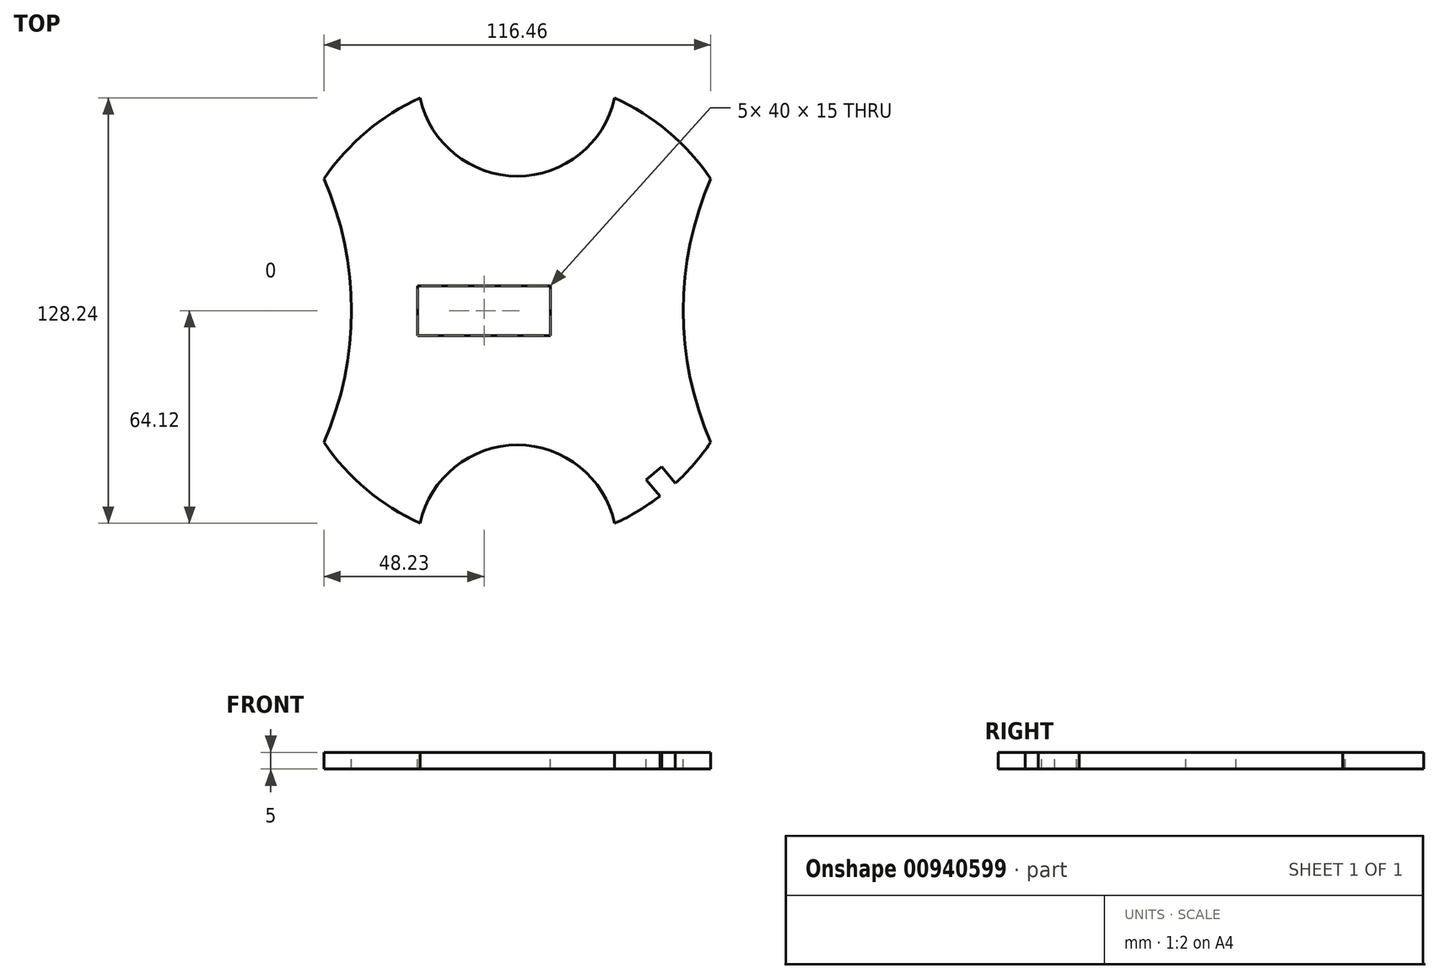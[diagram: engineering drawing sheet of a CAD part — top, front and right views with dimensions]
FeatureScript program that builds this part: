
annotation { "Feature Type Name" : "Feature", "Feature Type Description" : "" }
export const myFeature = defineFeature(function(context is Context, id is Id, definition is map)
    precondition{}
    {
        {
            var Q0;
            Q0=qCreatedBy(makeId("Top.planeOp"),FACE);
            var sketch = newSketch(context, id + "F0", { "sketchPlane" : qUnion([Q0])});
            skCircle(sketch, "E0", {"center": v(0, 0) * mm, "radius": 70.5 * mm});
            skSolve(sketch);
        }
        {
            var Q0;
            Q0 = qSketchRegion(id + "F0", true);
            extrude(context, id + "F1", {"entities" : qUnion([Q0]), "depth" : 5 * mm, "offsetDistance" : 25 * mm});
        }
        {
            var Q0;
            Q0=makeQuery(id+"F1.opExtrude","CAP_FACE",FACE,{"disambiguationData":[OSD([sQuery(id+"F0.wireOp",EDGE,"E0")])],"isStart":false});
            var sketch = newSketch(context, id + "F2", { "sketchPlane" : qUnion([Q0])});
            skLineSegment(sketch, "E1.bottom", {"start": v(-30, 7.5) * mm, "end": v(10, 7.5) * mm});
            skLineSegment(sketch, "E1.top", {"start": v(-30, -7.5) * mm, "end": v(10, -7.5) * mm});
            skLineSegment(sketch, "E1.left", {"start": v(-30, 7.5) * mm, "end": v(-30, -7.5) * mm});
            skLineSegment(sketch, "E1.right", {"start": v(10, 7.5) * mm, "end": v(10, -7.5) * mm});
            skSolve(sketch);
        }
        {
            var Q0;
            Q0 = qSketchRegion(id + "F2", true);
            extrude(context, id + "F3", {"entities" : qUnion([Q0]), "operationType" : NewBodyOperationType.REMOVE, "oppositeDirection" : true, "depth" : 25 * mm, "offsetDistance" : 25 * mm});
        }
        {
            var Q0;
            Q0=makeQuery(id+"F1.opExtrude","CAP_FACE",FACE,{"disambiguationData":[OSD([sQuery(id+"F0.wireOp",EDGE,"E0")])],"isStart":false});
            var sketch = newSketch(context, id + "F4", { "sketchPlane" : qUnion([Q0])});
            skLineSegment(sketch, "E2", {"start": v(0, -70.5) * mm, "end": v(0, 70.5) * mm, "construction": true});
            skCircle(sketch, "E3", {"center": v(0, 70.5) * mm, "radius": 30 * mm});
            skCircle(sketch, "E4", {"center": v(0, -70.5) * mm, "radius": 30 * mm});
            skLineSegment(sketch, "E5", {"start": v(-150, 0) * mm, "end": v(150, 0) * mm, "construction": true});
            skCircle(sketch, "E6", {"center": v(150, 0) * mm, "radius": 100 * mm});
            skCircle(sketch, "E7", {"center": v(-150, 0) * mm, "radius": 100 * mm});
            skSolve(sketch);
        }
        {
            var Q0;
            {var subQ0=sQuery(id+"F4.wireOp",EDGE,"E3");var subQ1=makeQuery(id+"F1.opExtrude","CAP_EDGE",EDGE,{"disambiguationData":[OSD([sQuery(id+"F0.wireOp",EDGE,"E0")])],"isStart":false});var subQ2=makeQuery(id+"F4.imprint","INTERSECT",VERTEX,{"disambiguationData":[OD(0.0)],"derivedFrom":[subQ1,subQ0]});Q0=makeQuery(id+"F4.imprint","IMPRINT",FACE,{"disambiguationData":[TD([[makeQuery(id+"F4.imprint","IMPRINT",EDGE,{"disambiguationData":[TD([[subQ2,-1.0]])],"derivedFrom":subQ0}),1.0]])]});}
            var Q1;
            {var subQ0=sQuery(id+"F4.wireOp",EDGE,"E7");var subQ1=makeQuery(id+"F1.opExtrude","CAP_EDGE",EDGE,{"disambiguationData":[OSD([sQuery(id+"F0.wireOp",EDGE,"E0")])],"isStart":false});var subQ2=makeQuery(id+"F4.imprint","INTERSECT",VERTEX,{"disambiguationData":[OD(0.0)],"derivedFrom":[subQ1,subQ0]});Q1=makeQuery(id+"F4.imprint","IMPRINT",FACE,{"disambiguationData":[TD([[makeQuery(id+"F4.imprint","IMPRINT",EDGE,{"disambiguationData":[TD([[subQ2,-1.0]])],"derivedFrom":subQ0}),1.0]])]});}
            var Q2;
            {var subQ0=sQuery(id+"F4.wireOp",EDGE,"E4");var subQ1=makeQuery(id+"F1.opExtrude","CAP_EDGE",EDGE,{"disambiguationData":[OSD([sQuery(id+"F0.wireOp",EDGE,"E0")])],"isStart":false});var subQ2=makeQuery(id+"F4.imprint","INTERSECT",VERTEX,{"disambiguationData":[OD(0.0)],"derivedFrom":[subQ1,subQ0]});Q2=makeQuery(id+"F4.imprint","IMPRINT",FACE,{"disambiguationData":[TD([[makeQuery(id+"F4.imprint","IMPRINT",EDGE,{"disambiguationData":[TD([[subQ2,1.0]])],"derivedFrom":subQ0}),1.0]])]});}
            var Q3;
            {var subQ0=sQuery(id+"F4.wireOp",EDGE,"E6");var subQ1=makeQuery(id+"F1.opExtrude","CAP_EDGE",EDGE,{"disambiguationData":[OSD([sQuery(id+"F0.wireOp",EDGE,"E0")])],"isStart":false});var subQ2=makeQuery(id+"F4.imprint","INTERSECT",VERTEX,{"disambiguationData":[OD(0.0)],"derivedFrom":[subQ1,subQ0]});Q3=makeQuery(id+"F4.imprint","IMPRINT",FACE,{"disambiguationData":[TD([[makeQuery(id+"F4.imprint","IMPRINT",EDGE,{"disambiguationData":[TD([[subQ2,1.0]])],"derivedFrom":subQ0}),1.0]])]});}
            extrude(context, id + "F5", {"entities" : qUnion([Q0, Q1, Q2, Q3]), "operationType" : NewBodyOperationType.REMOVE, "oppositeDirection" : true, "depth" : 25 * mm, "offsetDistance" : 25 * mm});
        }
        {
            var Q0;
            Q0=makeQuery(id+"F1.opExtrude","CAP_FACE",FACE,{"disambiguationData":[OSD([sQuery(id+"F0.wireOp",EDGE,"E0")])],"isStart":false});
            var sketch = newSketch(context, id + "F6", { "sketchPlane" : qUnion([Q0])});
            skCircle(sketch, "E8", {"center": v(0, 0) * mm, "radius": 70.5 * mm});
            skLineSegment(sketch, "E9.0", {"start": v(38.84, -50.96) * mm, "end": v(44.95, -58.23) * mm});
            skLineSegment(sketch, "E10.0", {"start": v(43.44, -47.1) * mm, "end": v(49.54, -54.38) * mm});
            skLineSegment(sketch, "E11", {"start": v(38.84, -50.96) * mm, "end": v(43.44, -47.1) * mm});
            skLineSegment(sketch, "E12", {"start": v(44.95, -58.23) * mm, "end": v(50.4, -59.42) * mm});
            skLineSegment(sketch, "E13", {"start": v(50.4, -59.42) * mm, "end": v(49.54, -54.38) * mm});
            skSolve(sketch);
        }
        {
            var Q0;
            {var subQ5=sQuery(id+"F6.wireOp",EDGE,"E11");Q0=makeQuery(id+"F6.imprint","IMPRINT",FACE,{"disambiguationData":[TD([[makeQuery(id+"F6.imprint","IMPRINT",EDGE,{"derivedFrom":subQ5}),-1.0]])]});}
            extrude(context, id + "F7", {"entities" : qUnion([Q0]), "operationType" : NewBodyOperationType.REMOVE, "oppositeDirection" : true, "depth" : 25 * mm, "offsetDistance" : 25 * mm});
        }
    });
